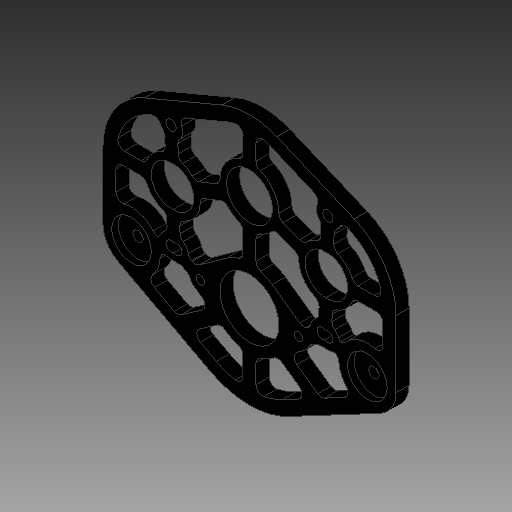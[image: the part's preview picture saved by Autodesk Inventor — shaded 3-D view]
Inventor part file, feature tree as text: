
AUTODESK INVENTOR PART (.ipt)
format: ipt  version: 2019 (Build 230136000, 136)  size: 399,360 bytes
history: native  units: in
note: dims shown in document units (in); Inventor stores cm internally (conversion verified against a paired STEP export)
features: mirror x1
ambient origin geometry x8: Origin, YZ Plane, XZ Plane, XY Plane, X Axis, Y Axis, Z Axis, Center Point
bodies: Solid1 (feature_tree)
feature tree (1):
  mirror  "Mirror1"
